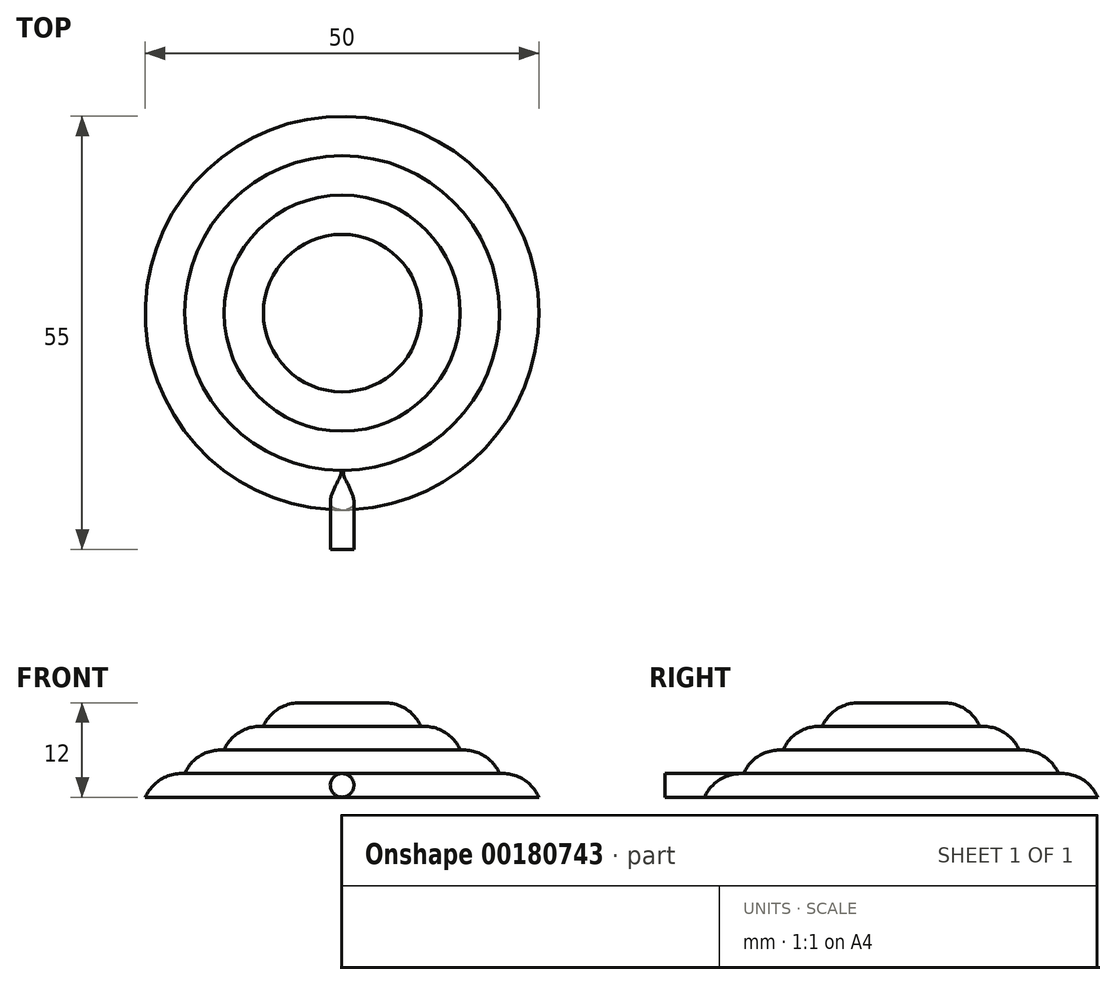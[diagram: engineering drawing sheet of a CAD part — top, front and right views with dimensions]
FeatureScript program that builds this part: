
annotation { "Feature Type Name" : "Feature", "Feature Type Description" : "" }
export const myFeature = defineFeature(function(context is Context, id is Id, definition is map)
    precondition{}
    {
        {
            var Q0;
            Q0=qCreatedBy(makeId("Top.planeOp"),FACE);
            var sketch = newSketch(context, id + "F0", { "sketchPlane" : qUnion([Q0])});
            skCircle(sketch, "E0", {"center": v(0, 0) * mm, "radius": 25 * mm});
            skSolve(sketch);
        }
        {
            var Q0;
            Q0=qCreatedBy(makeId("Top.planeOp"),FACE);
            var sketch = newSketch(context, id + "F1", { "sketchPlane" : qUnion([Q0])});
            skCircle(sketch, "E1", {"center": v(0, 0) * mm, "radius": 20 * mm});
            skSolve(sketch);
        }
        {
            var Q0;
            Q0 = qSketchRegion(id + "F0", true);
            extrude(context, id + "F2", {"entities" : qUnion([Q0]), "depth" : 3 * mm});
        }
        {
            var Q0;
            Q0 = qSketchRegion(id + "F1", true);
            extrude(context, id + "F3", {"entities" : qUnion([Q0]), "operationType" : NewBodyOperationType.ADD, "depth" : 6 * mm});
        }
        {
            var Q0;
            Q0=qCreatedBy(makeId("Top.planeOp"),FACE);
            var sketch = newSketch(context, id + "F4", { "sketchPlane" : qUnion([Q0])});
            skCircle(sketch, "E2", {"center": v(0, 0) * mm, "radius": 15 * mm});
            skSolve(sketch);
        }
        {
            var Q0;
            Q0 = qSketchRegion(id + "F4", true);
            extrude(context, id + "F5", {"entities" : qUnion([Q0]), "operationType" : NewBodyOperationType.ADD, "depth" : 9 * mm});
        }
        {
            var Q0;
            Q0=qCreatedBy(makeId("Top.planeOp"),FACE);
            var sketch = newSketch(context, id + "F6", { "sketchPlane" : qUnion([Q0])});
            skCircle(sketch, "E3", {"center": v(0, 0) * mm, "radius": 10 * mm});
            skSolve(sketch);
        }
        {
            var Q0;
            Q0 = qSketchRegion(id + "F6", true);
            extrude(context, id + "F7", {"entities" : qUnion([Q0]), "operationType" : NewBodyOperationType.ADD, "depth" : 12 * mm});
        }
        {
            var Q0;
            Q0=makeQuery(id+"F7.opExtrude","CAP_EDGE",EDGE,{"disambiguationData":[OSD([sQuery(id+"F6.wireOp",EDGE,"E3")])],"isStart":false});
            fillet(context, id + "F8", {"entities" : qUnion([Q0]), "radius" : 5 * mm, "tangentPropagation" : true, "allowEdgeOverflow" : false});
        }
        {
            var Q0;
            Q0=makeQuery(id+"F5.opExtrude","CAP_EDGE",EDGE,{"disambiguationData":[OSD([sQuery(id+"F4.wireOp",EDGE,"E2")])],"isStart":false});
            fillet(context, id + "F9", {"entities" : qUnion([Q0]), "radius" : 5 * mm, "tangentPropagation" : true, "allowEdgeOverflow" : false});
        }
        {
            var Q0;
            Q0=makeQuery(id+"F3.opExtrude","CAP_EDGE",EDGE,{"disambiguationData":[OSD([sQuery(id+"F1.wireOp",EDGE,"E1")])],"isStart":false});
            fillet(context, id + "F10", {"entities" : qUnion([Q0]), "radius" : 5 * mm, "tangentPropagation" : true, "allowEdgeOverflow" : false});
        }
        {
            var Q0;
            Q0=makeQuery(id+"F2.opExtrude","CAP_EDGE",EDGE,{"disambiguationData":[OSD([sQuery(id+"F0.wireOp",EDGE,"E0")])],"isStart":false});
            fillet(context, id + "F11", {"entities" : qUnion([Q0]), "radius" : 5 * mm, "tangentPropagation" : true, "allowEdgeOverflow" : false});
        }
        {
            var Q0;
            Q0=qCreatedBy(makeId("Front.planeOp"),FACE);
            var sketch = newSketch(context, id + "F12", { "sketchPlane" : qUnion([Q0])});
            skCircle(sketch, "E4", {"center": v(0, 1.5) * mm, "radius": 1.5 * mm});
            skSolve(sketch);
        }
        {
            var Q0;
            Q0 = qSketchRegion(id + "F12", true);
            extrude(context, id + "F13", {"entities" : qUnion([Q0]), "operationType" : NewBodyOperationType.ADD, "depth" : 30 * mm});
        }
    });
